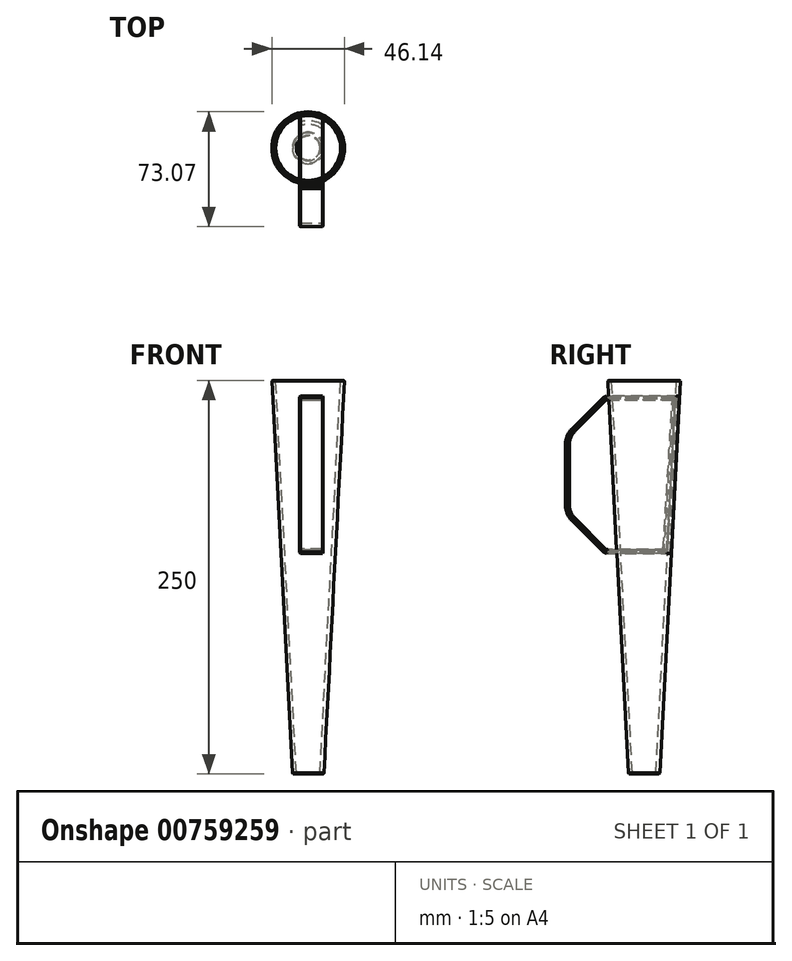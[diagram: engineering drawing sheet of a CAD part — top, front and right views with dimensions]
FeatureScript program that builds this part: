
annotation { "Feature Type Name" : "Feature", "Feature Type Description" : "" }
export const myFeature = defineFeature(function(context is Context, id is Id, definition is map)
    precondition{}
    {
        {
            var Q0;
            Q0=qCreatedBy(makeId("Top.planeOp"),FACE);
            var sketch = newSketch(context, id + "F0", { "sketchPlane" : qUnion([Q0])});
            skCircle(sketch, "E0", {"center": v(0, 0) * mm, "radius": 10 * mm});
            skSolve(sketch);
        }
        {
            var Q0;
            Q0=makeQuery(id+"F0.imprint","IMPRINT",FACE,{"disambiguationData":[TD([[makeQuery(id+"F0.imprint","IMPRINT",EDGE,{"derivedFrom":sQuery(id+"F0.wireOp",EDGE,"E0")}),1.0]])]});
            extrude(context, id + "F1", {"entities" : qUnion([Q0]), "depth" : 250 * mm, "offsetDistance" : 25 * mm, "hasDraft" : true, "draftAngle" : 3 * degree});
        }
        {
            var Q0;
            Q0=qCreatedBy(makeId("Front.planeOp"),FACE);
            var sketch = newSketch(context, id + "F2", { "sketchPlane" : qUnion([Q0])});
            skLineSegment(sketch, "E1.bottom", {"start": v(-5.41, 240) * mm, "end": v(9.59, 240) * mm});
            skLineSegment(sketch, "E1.top", {"start": v(-5.41, 140) * mm, "end": v(9.59, 140) * mm});
            skLineSegment(sketch, "E1.left", {"start": v(-5.41, 240) * mm, "end": v(-5.41, 140) * mm});
            skLineSegment(sketch, "E1.right", {"start": v(9.59, 240) * mm, "end": v(9.59, 140) * mm});
            skSolve(sketch);
        }
        {
            var Q0;
            Q0 = qSketchRegion(id + "F2", true);
            var Q1;
            Q1=makeQuery(id+"F1.opExtrude","SWEPT_FACE",FACE,{"disambiguationData":[OSD([sQuery(id+"F0.wireOp",EDGE,"E0")])]});
            var Q2;
            Q2=makeQuery(id+"F1.opExtrude","SWEPT_FACE",FACE,{"disambiguationData":[OSD([sQuery(id+"F0.wireOp",EDGE,"E0")])]});
            var Q3;
            Q3=makeQuery(id+"F1.opExtrude","SWEPT_BODY",BODY,{"disambiguationData":[OSD([sQuery(id+"F0.wireOp",EDGE,"E0")])]});
            extrude(context, id + "F3", {"entities" : qUnion([Q0]), "endBound" : BoundingType.UP_TO_SURFACE, "oppositeDirection" : true, "depth" : 50 * mm, "endBoundEntityFace" : qUnion([Q1]), "offsetDistance" : 50 * mm, "hasSecondDirection" : true, "secondDirectionOppositeDirection" : false, "secondDirectionDepth" : 50 * mm, "secondDirectionBoundEntityFace" : qUnion([Q2]), "secondDirectionBoundEntityBody" : qUnion([Q3]), "hasSecondDirectionOffset" : true, "secondDirectionOffsetDistance" : 25 * mm});
        }
        {
            var Q0;
            Q0=makeQuery(id+"F3.opExtrude","CAP_EDGE",EDGE,{"disambiguationData":[OSD([sQuery(id+"F2.wireOp",EDGE,"E1.top")])],"isStart":true});
            var Q1;
            Q1=makeQuery(id+"F3.opExtrude","CAP_EDGE",EDGE,{"disambiguationData":[OSD([sQuery(id+"F2.wireOp",EDGE,"E1.bottom")])],"isStart":true});
            chamfer(context, id + "F4", {"entities" : qUnion([Q0, Q1]), "width" : 25 * mm, "tangentPropagation" : true});
        }
        {
            var Q0;
            {var subQ0=sQuery(id+"F2.wireOp",EDGE,"E1.top");Q0=makeQuery(id+"F4.opChamfer","BLEND_EDGE",EDGE,{"blendedFrom":[makeQuery(id+"F3.opExtrude","CAP_EDGE",EDGE,{"disambiguationData":[OSD([subQ0])],"isStart":true}),makeQuery(id+"F3.opExtrude","SWEPT_FACE",FACE,{"disambiguationData":[OSD([subQ0])]})],"blendedInto":[makeQuery(id+"F3.opExtrude","SWEPT_FACE",FACE,{"disambiguationData":[OSD([subQ0])]})]});}
            var Q1;
            {var subQ0=sQuery(id+"F2.wireOp",EDGE,"E1.bottom");Q1=makeQuery(id+"F4.opChamfer","BLEND_EDGE",EDGE,{"blendedFrom":[makeQuery(id+"F3.opExtrude","CAP_EDGE",EDGE,{"disambiguationData":[OSD([subQ0])],"isStart":true}),makeQuery(id+"F3.opExtrude","SWEPT_FACE",FACE,{"disambiguationData":[OSD([subQ0])]})],"blendedInto":[makeQuery(id+"F3.opExtrude","SWEPT_FACE",FACE,{"disambiguationData":[OSD([subQ0])]})]});}
            chamfer(context, id + "F5", {"entities" : qUnion([Q0, Q1]), "width" : 3 * mm, "tangentPropagation" : true});
        }
        {
            var Q0;
            {var subQ0=sQuery(id+"F2.wireOp",EDGE,"E1.bottom");Q0=makeQuery(id+"F4.opChamfer","BLEND_EDGE",EDGE,{"blendedFrom":[makeQuery(id+"F3.opExtrude","CAP_EDGE",EDGE,{"disambiguationData":[OSD([subQ0])],"isStart":true}),makeQuery(id+"F3.opExtrude","CAP_FACE",FACE,{"disambiguationData":[OSD([subQ0,sQuery(id+"F2.wireOp",EDGE,"E1.top"),sQuery(id+"F2.wireOp",EDGE,"E1.left"),sQuery(id+"F2.wireOp",EDGE,"E1.right")])],"isStart":true})],"blendedInto":[makeQuery(id+"F3.opExtrude","CAP_FACE",FACE,{"disambiguationData":[OSD([subQ0,sQuery(id+"F2.wireOp",EDGE,"E1.top"),sQuery(id+"F2.wireOp",EDGE,"E1.left"),sQuery(id+"F2.wireOp",EDGE,"E1.right")])],"isStart":true})]});}
            var Q1;
            {var subQ0=sQuery(id+"F2.wireOp",EDGE,"E1.top");Q1=makeQuery(id+"F4.opChamfer","BLEND_EDGE",EDGE,{"blendedFrom":[makeQuery(id+"F3.opExtrude","CAP_EDGE",EDGE,{"disambiguationData":[OSD([subQ0])],"isStart":true}),makeQuery(id+"F3.opExtrude","CAP_FACE",FACE,{"disambiguationData":[OSD([sQuery(id+"F2.wireOp",EDGE,"E1.bottom"),subQ0,sQuery(id+"F2.wireOp",EDGE,"E1.left"),sQuery(id+"F2.wireOp",EDGE,"E1.right")])],"isStart":true})],"blendedInto":[makeQuery(id+"F3.opExtrude","CAP_FACE",FACE,{"disambiguationData":[OSD([sQuery(id+"F2.wireOp",EDGE,"E1.bottom"),subQ0,sQuery(id+"F2.wireOp",EDGE,"E1.left"),sQuery(id+"F2.wireOp",EDGE,"E1.right")])],"isStart":true})]});}
            fillet(context, id + "F6", {"entities" : qUnion([Q0, Q1]), "radius" : 15 * mm, "tangentPropagation" : true, "allowEdgeOverflow" : false});
        }
        {
            var Q0;
            Q0=makeQuery(id+"F3.opExtrude","SWEPT_FACE",FACE,{"disambiguationData":[OSD([sQuery(id+"F2.wireOp",EDGE,"E1.right")])]});
            var Q1;
            Q1=makeQuery(id+"F3.opExtrude","SWEPT_FACE",FACE,{"disambiguationData":[OSD([sQuery(id+"F2.wireOp",EDGE,"E1.left")])]});
            var Q2;
            Q2=makeQuery(id+"F3.opExtrude","SWEPT_BODY",BODY,{"disambiguationData":[OSD([sQuery(id+"F2.wireOp",EDGE,"E1.bottom"),sQuery(id+"F2.wireOp",EDGE,"E1.top"),sQuery(id+"F2.wireOp",EDGE,"E1.left"),sQuery(id+"F2.wireOp",EDGE,"E1.right")])]});
            shell(context, id + "F7", {"entities" : qUnion([Q0, Q1]), "parts" : qUnion([Q2]), "thickness" : 2.5 * mm});
        }
        {
            var Q0;
            Q0=makeQuery(id+"F3.opExtrude","SWEPT_FACE",FACE,{"disambiguationData":[OSD([sQuery(id+"F2.wireOp",EDGE,"E1.left")])]});
            var Q1;
            Q1=makeQuery(id+"F3.opExtrude","SWEPT_FACE",FACE,{"disambiguationData":[OSD([sQuery(id+"F2.wireOp",EDGE,"E1.right")])]});
            chamfer(context, id + "F8", {"entities" : qUnion([Q0, Q1]), "width" : 0.5 * mm, "tangentPropagation" : true});
        }
        {
            var Q0;
            Q0=makeQuery(id+"F1.opExtrude","CAP_FACE",FACE,{"disambiguationData":[OSD([sQuery(id+"F0.wireOp",EDGE,"E0")])],"isStart":false});
            var Q1;
            Q1=makeQuery(id+"F1.opExtrude","CAP_FACE",FACE,{"disambiguationData":[OSD([sQuery(id+"F0.wireOp",EDGE,"E0")])],"isStart":true});
            shell(context, id + "F9", {"entities" : qUnion([Q0, Q1]), "thickness" : 2.5 * mm});
        }
        {
            var Q0;
            Q0=makeQuery(id+"F1.opExtrude","CAP_FACE",FACE,{"disambiguationData":[OSD([sQuery(id+"F0.wireOp",EDGE,"E0")])],"isStart":true});
            var Q1;
            Q1=makeQuery(id+"F1.opExtrude","CAP_FACE",FACE,{"disambiguationData":[OSD([sQuery(id+"F0.wireOp",EDGE,"E0")])],"isStart":false});
            chamfer(context, id + "F10", {"entities" : qUnion([Q0, Q1]), "width" : 0.5 * mm, "tangentPropagation" : true});
        }
    });
